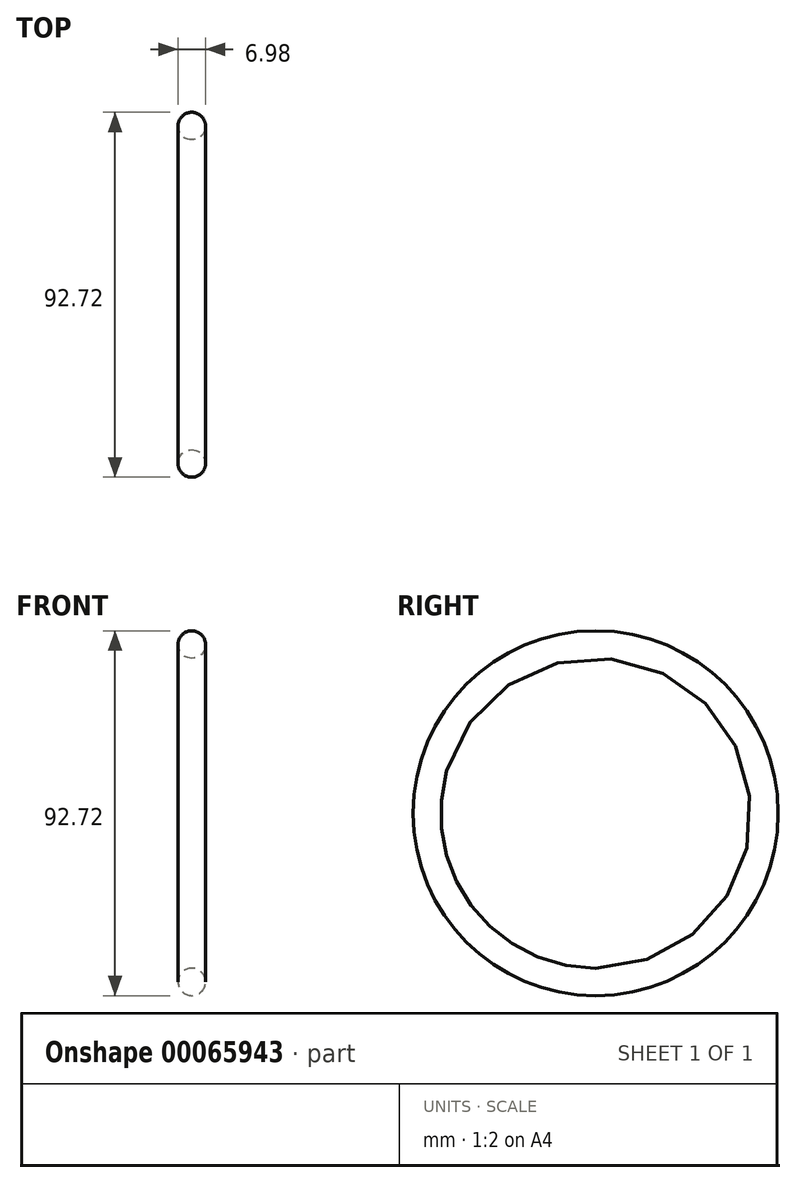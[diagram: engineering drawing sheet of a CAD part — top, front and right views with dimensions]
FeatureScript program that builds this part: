
annotation { "Feature Type Name" : "Feature", "Feature Type Description" : "" }
export const myFeature = defineFeature(function(context is Context, id is Id, definition is map)
    precondition{}
    {
        {
            var Q0;
            Q0=qCreatedBy(makeId("Front.planeOp"),FACE);
            var sketch = newSketch(context, id + "F0", { "sketchPlane" : qUnion([Q0])});
            skLineSegment(sketch, "E0", {"start": v(0, 0) * mm, "end": v(-6.06, 0) * mm, "construction": true});
            skCircle(sketch, "E1", {"center": v(0, 42.86) * mm, "radius": 3.5 * mm});
            skSolve(sketch);
        }
        {
            var Q0;
            Q0=makeQuery(id+"F0.imprint","IMPRINT",FACE,{"disambiguationData":[TD([[makeQuery(id+"F0.imprint","IMPRINT",EDGE,{"derivedFrom":sQuery(id+"F0.wireOp",EDGE,"E1")}),1.0]])]});
            var Q1;
            Q1=sQuery(id+"F0.wireOp",EDGE,"E0");
            revolve(context, id + "F1", {"entities" : qUnion([Q0]), "axis" : qUnion([Q1]), "revolveType" : RevolveType.FULL});
        }
    });
